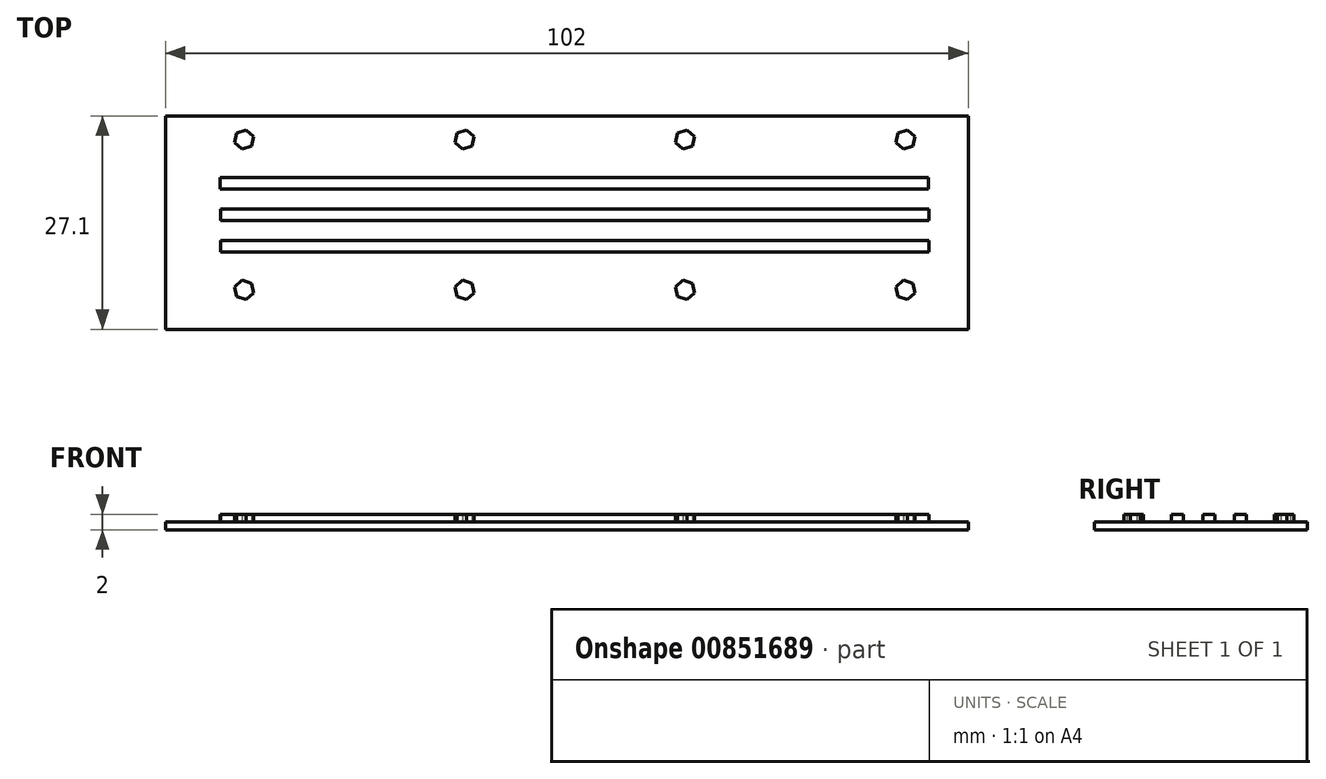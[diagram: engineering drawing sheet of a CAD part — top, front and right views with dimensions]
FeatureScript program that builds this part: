
annotation { "Feature Type Name" : "Feature", "Feature Type Description" : "" }
export const myFeature = defineFeature(function(context is Context, id is Id, definition is map)
    precondition{}
    {
        {
            var Q0;
            Q0=qCreatedBy(makeId("Top.planeOp"),FACE);
            var sketch = newSketch(context, id + "F0", { "sketchPlane" : qUnion([Q0])});
            skLineSegment(sketch, "E0.bottom", {"start": v(50, -14.55) * mm, "end": v(-52, -14.55) * mm});
            skLineSegment(sketch, "E0.top", {"start": v(50, 12.55) * mm, "end": v(-52, 12.55) * mm});
            skLineSegment(sketch, "E0.left", {"start": v(50, -14.55) * mm, "end": v(50, 12.55) * mm});
            skLineSegment(sketch, "E0.right", {"start": v(-52, -14.55) * mm, "end": v(-52, 12.55) * mm});
            skLineSegment(sketch, "E1.MirrorCS", {"start": v(-126.2, 15.84) * mm, "end": v(-126.2, -15.96) * mm, "construction": true});
            skSolve(sketch);
        }
        {
            var Q0;
            Q0=makeQuery(id+"F0.imprint","IMPRINT",FACE,{"disambiguationData":[TD([[makeQuery(id+"F0.imprint","IMPRINT",EDGE,{"derivedFrom":sQuery(id+"F0.wireOp",EDGE,"E0.bottom")}),-1.0]])]});
            extrude(context, id + "F1", {"entities" : qUnion([Q0]), "depth" : 1 * mm, "offsetDistance" : 25 * mm});
        }
        {
            var Q0;
            Q0=makeQuery(id+"F1.opExtrude","CAP_FACE",FACE,{"disambiguationData":[OSD([sQuery(id+"F0.wireOp",EDGE,"E0.bottom"),sQuery(id+"F0.wireOp",EDGE,"E0.top"),sQuery(id+"F0.wireOp",EDGE,"E0.left"),sQuery(id+"F0.wireOp",EDGE,"E0.right"),sQuery(id+"F0.wireOp",EDGE,"f0fb288a-a811-4cf8-ac7b-5b0ab74712d8.0.1.0"),sQuery(id+"F0.wireOp",EDGE,"f0fb288a-a811-4cf8-ac7b-5b0ab74712d8.0.1.2"),sQuery(id+"F0.wireOp",EDGE,"f0fb288a-a811-4cf8-ac7b-5b0ab74712d8.0.1.3"),sQuery(id+"F0.wireOp",EDGE,"f0fb288a-a811-4cf8-ac7b-5b0ab74712d8.0.2.0"),sQuery(id+"F0.wireOp",EDGE,"f0fb288a-a811-4cf8-ac7b-5b0ab74712d8.0.2.2"),sQuery(id+"F0.wireOp",EDGE,"f0fb288a-a811-4cf8-ac7b-5b0ab74712d8.0.2.3"),sQuery(id+"F0.wireOp",EDGE,"f0fb288a-a811-4cf8-ac7b-5b0ab74712d8.0.3.0"),sQuery(id+"F0.wireOp",EDGE,"f0fb288a-a811-4cf8-ac7b-5b0ab74712d8.0.3.2"),sQuery(id+"F0.wireOp",EDGE,"f0fb288a-a811-4cf8-ac7b-5b0ab74712d8.0.3.3"),sQuery(id+"F0.wireOp",EDGE,"f0fb288a-a811-4cf8-ac7b-5b0ab74712d8.0.4.0"),sQuery(id+"F0.wireOp",EDGE,"f0fb288a-a811-4cf8-ac7b-5b0ab74712d8.0.4.2"),sQuery(id+"F0.wireOp",EDGE,"f0fb288a-a811-4cf8-ac7b-5b0ab74712d8.0.4.3"),sQuery(id+"F0.wireOp",EDGE,"RKnVQM72-ZrRu-pSdJ-AaKB-wKwvzhgqjjUU"),sQuery(id+"F0.wireOp",EDGE,"7q8Byt5Z-z77J-wEaE-JFo7-deLDxunnqvEf"),sQuery(id+"F0.wireOp",EDGE,"hnmrVM6Z-fPP9-FfmX-qtFs-U7qnaTaGnJsT"),sQuery(id+"F0.wireOp",EDGE,"2AhRkgEB-YtaR-VW2O-F7jD-dwlzht8Cownv")])],"isStart":false});
            var sketch = newSketch(context, id + "F2", { "sketchPlane" : qUnion([Q0])});
            skCircle(sketch, "E2.cCircle", {"center": v(-42, 9.55) * mm, "radius": 1.25 * mm, "construction": true});
            skLineSegment(sketch, "E2.0", {"start": v(-41.07, 8.72) * mm, "end": v(-42.25, 8.33) * mm});
            skLineSegment(sketch, "E2.1", {"start": v(-42.25, 8.33) * mm, "end": v(-43.19, 9.16) * mm});
            skLineSegment(sketch, "E2.2", {"start": v(-43.19, 9.16) * mm, "end": v(-42.93, 10.38) * mm});
            skLineSegment(sketch, "E2.3", {"start": v(-42.93, 10.38) * mm, "end": v(-41.75, 10.77) * mm});
            skLineSegment(sketch, "E2.4", {"start": v(-41.75, 10.77) * mm, "end": v(-40.81, 9.94) * mm});
            skLineSegment(sketch, "E2.5", {"start": v(-40.81, 9.94) * mm, "end": v(-41.07, 8.72) * mm});
            skLineSegment(sketch, "E3.1.0.0", {"start": v(-12.81, 9.94) * mm, "end": v(-13.07, 8.72) * mm});
            skLineSegment(sketch, "E3.1.0.1", {"start": v(-13.75, 10.77) * mm, "end": v(-12.81, 9.94) * mm});
            skLineSegment(sketch, "E3.1.0.2", {"start": v(-14.93, 10.38) * mm, "end": v(-13.75, 10.77) * mm});
            skLineSegment(sketch, "E3.1.0.3", {"start": v(-15.19, 9.16) * mm, "end": v(-14.93, 10.38) * mm});
            skLineSegment(sketch, "E3.1.0.4", {"start": v(-14.25, 8.33) * mm, "end": v(-15.19, 9.16) * mm});
            skLineSegment(sketch, "E3.1.0.5", {"start": v(-13.07, 8.72) * mm, "end": v(-14.25, 8.33) * mm});
            skCircle(sketch, "E3.1.0.6", {"center": v(-14, 9.55) * mm, "radius": 1.25 * mm, "construction": true});
            skLineSegment(sketch, "E3.2.0.0", {"start": v(15.19, 9.94) * mm, "end": v(14.93, 8.72) * mm});
            skLineSegment(sketch, "E3.2.0.1", {"start": v(14.25, 10.77) * mm, "end": v(15.19, 9.94) * mm});
            skLineSegment(sketch, "E3.2.0.2", {"start": v(13.07, 10.38) * mm, "end": v(14.25, 10.77) * mm});
            skLineSegment(sketch, "E3.2.0.3", {"start": v(12.81, 9.16) * mm, "end": v(13.07, 10.38) * mm});
            skLineSegment(sketch, "E3.2.0.4", {"start": v(13.75, 8.33) * mm, "end": v(12.81, 9.16) * mm});
            skLineSegment(sketch, "E3.2.0.5", {"start": v(14.93, 8.72) * mm, "end": v(13.75, 8.33) * mm});
            skCircle(sketch, "E3.2.0.6", {"center": v(14, 9.55) * mm, "radius": 1.25 * mm, "construction": true});
            skLineSegment(sketch, "E3.3.0.0", {"start": v(43.19, 9.94) * mm, "end": v(42.93, 8.72) * mm});
            skLineSegment(sketch, "E3.3.0.1", {"start": v(42.25, 10.77) * mm, "end": v(43.19, 9.94) * mm});
            skLineSegment(sketch, "E3.3.0.2", {"start": v(41.07, 10.38) * mm, "end": v(42.25, 10.77) * mm});
            skLineSegment(sketch, "E3.3.0.3", {"start": v(40.81, 9.16) * mm, "end": v(41.07, 10.38) * mm});
            skLineSegment(sketch, "E3.3.0.4", {"start": v(41.75, 8.33) * mm, "end": v(40.81, 9.16) * mm});
            skLineSegment(sketch, "E3.3.0.5", {"start": v(42.93, 8.72) * mm, "end": v(41.75, 8.33) * mm});
            skCircle(sketch, "E3.3.0.6", {"center": v(42, 9.55) * mm, "radius": 1.25 * mm, "construction": true});
            skLineSegment(sketch, "E3.direction1", {"start": v(-41.07, 8.72) * mm, "end": v(-13.07, 8.72) * mm, "construction": true});
            skLineSegment(sketch, "E4.MirrorCS", {"start": v(-42.93, -10.38) * mm, "end": v(-41.75, -10.77) * mm});
            skLineSegment(sketch, "E5.MirrorCS", {"start": v(-15.19, -9.16) * mm, "end": v(-14.93, -10.38) * mm});
            skLineSegment(sketch, "E6.MirrorCS", {"start": v(41.75, -8.33) * mm, "end": v(40.81, -9.16) * mm});
            skLineSegment(sketch, "E7.MirrorCS", {"start": v(42.25, -10.77) * mm, "end": v(43.19, -9.94) * mm});
            skLineSegment(sketch, "E8.MirrorCS", {"start": v(12.81, -9.16) * mm, "end": v(13.07, -10.38) * mm});
            skLineSegment(sketch, "E9.MirrorCS", {"start": v(40.81, -9.16) * mm, "end": v(41.07, -10.38) * mm});
            skLineSegment(sketch, "E10.MirrorCS", {"start": v(13.07, -10.38) * mm, "end": v(14.25, -10.77) * mm});
            skLineSegment(sketch, "E11.MirrorCS", {"start": v(-14.25, -8.33) * mm, "end": v(-15.19, -9.16) * mm});
            skLineSegment(sketch, "E12.MirrorCS", {"start": v(-14.93, -10.38) * mm, "end": v(-13.75, -10.77) * mm});
            skLineSegment(sketch, "E13.MirrorCS", {"start": v(41.07, -10.38) * mm, "end": v(42.25, -10.77) * mm});
            skLineSegment(sketch, "E14.MirrorCS", {"start": v(-43.19, -9.16) * mm, "end": v(-42.93, -10.38) * mm});
            skLineSegment(sketch, "E15.MirrorCS", {"start": v(-42.25, -8.33) * mm, "end": v(-43.19, -9.16) * mm});
            skLineSegment(sketch, "E16.MirrorCS", {"start": v(13.75, -8.33) * mm, "end": v(12.81, -9.16) * mm});
            skLineSegment(sketch, "E17.MirrorCS", {"start": v(14.25, -10.77) * mm, "end": v(15.19, -9.94) * mm});
            skLineSegment(sketch, "E18.MirrorCS", {"start": v(-13.75, -10.77) * mm, "end": v(-12.81, -9.94) * mm});
            skLineSegment(sketch, "E19.MirrorCS", {"start": v(-41.75, -10.77) * mm, "end": v(-40.81, -9.94) * mm});
            skLineSegment(sketch, "E20.MirrorCS", {"start": v(-41.07, -8.72) * mm, "end": v(-42.25, -8.33) * mm});
            skLineSegment(sketch, "E21.MirrorCS", {"start": v(-13.07, -8.72) * mm, "end": v(-14.25, -8.33) * mm});
            skLineSegment(sketch, "E22.MirrorCS", {"start": v(-40.81, -9.94) * mm, "end": v(-41.07, -8.72) * mm});
            skLineSegment(sketch, "E23.MirrorCS", {"start": v(15.19, -9.94) * mm, "end": v(14.93, -8.72) * mm});
            skCircle(sketch, "E24.MirrorC", {"center": v(-14, -9.55) * mm, "radius": 1.25 * mm, "construction": true});
            skLineSegment(sketch, "E25.MirrorCS", {"start": v(43.19, -9.94) * mm, "end": v(42.93, -8.72) * mm});
            skCircle(sketch, "E26.MirrorC", {"center": v(14, -9.55) * mm, "radius": 1.25 * mm, "construction": true});
            skCircle(sketch, "E27.MirrorC", {"center": v(42, -9.55) * mm, "radius": 1.25 * mm, "construction": true});
            skLineSegment(sketch, "E28.MirrorCS", {"start": v(-41.07, -8.72) * mm, "end": v(-13.07, -8.72) * mm, "construction": true});
            skCircle(sketch, "E29.MirrorC", {"center": v(-42, -9.55) * mm, "radius": 1.25 * mm, "construction": true});
            skLineSegment(sketch, "E30.MirrorCS", {"start": v(-12.81, -9.94) * mm, "end": v(-13.07, -8.72) * mm});
            skLineSegment(sketch, "E31.MirrorCS", {"start": v(14.93, -8.72) * mm, "end": v(13.75, -8.33) * mm});
            skLineSegment(sketch, "E32.MirrorCS", {"start": v(42.93, -8.72) * mm, "end": v(41.75, -8.33) * mm});
            skLineSegment(sketch, "E33.bottom", {"start": v(45, 0.75) * mm, "end": v(-45, 0.75) * mm});
            skLineSegment(sketch, "E33.top", {"start": v(45, -0.75) * mm, "end": v(-45, -0.75) * mm});
            skLineSegment(sketch, "E33.left", {"start": v(45, 0.75) * mm, "end": v(45, -0.75) * mm});
            skLineSegment(sketch, "E33.right", {"start": v(-45, 0.75) * mm, "end": v(-45, -0.75) * mm});
            skPoint(sketch, "E33.middle", {"position": v(0, 0) * mm});
            skLineSegment(sketch, "E34.1.0.0", {"start": v(45, -3.25) * mm, "end": v(-45, -3.25) * mm});
            skLineSegment(sketch, "E34.1.0.1", {"start": v(-45, -3.25) * mm, "end": v(-45, -4.75) * mm});
            skLineSegment(sketch, "E34.1.0.2", {"start": v(45, -4.75) * mm, "end": v(-45, -4.75) * mm});
            skLineSegment(sketch, "E34.1.0.3", {"start": v(45, -3.25) * mm, "end": v(45, -4.75) * mm});
            skLineSegment(sketch, "E35.1.0.1", {"start": v(44.93, 3.25) * mm, "end": v(-45.07, 3.25) * mm});
            skLineSegment(sketch, "E35.1.0.2", {"start": v(44.93, 4.75) * mm, "end": v(-45.07, 4.75) * mm});
            skLineSegment(sketch, "E35.1.0.3", {"start": v(44.93, 4.75) * mm, "end": v(44.93, 3.25) * mm});
            skLineSegment(sketch, "E36", {"start": v(-45.07, 4.75) * mm, "end": v(-45.07, 3.25) * mm});
            skSolve(sketch);
        }
        {
            var Q0;
            Q0=makeQuery(id+"F2.imprint","IMPRINT",FACE,{"disambiguationData":[TD([[makeQuery(id+"F2.imprint","IMPRINT",EDGE,{"derivedFrom":sQuery(id+"F2.wireOp",EDGE,"E2.0")}),-1.0]])]});
            var Q1;
            Q1=makeQuery(id+"F2.imprint","IMPRINT",FACE,{"disambiguationData":[TD([[makeQuery(id+"F2.imprint","IMPRINT",EDGE,{"derivedFrom":sQuery(id+"F2.wireOp",EDGE,"E3.1.0.0")}),-1.0]])]});
            var Q2;
            Q2=makeQuery(id+"F2.imprint","IMPRINT",FACE,{"disambiguationData":[TD([[makeQuery(id+"F2.imprint","IMPRINT",EDGE,{"derivedFrom":sQuery(id+"F2.wireOp",EDGE,"E3.2.0.0")}),-1.0]])]});
            var Q3;
            Q3=makeQuery(id+"F2.imprint","IMPRINT",FACE,{"disambiguationData":[TD([[makeQuery(id+"F2.imprint","IMPRINT",EDGE,{"derivedFrom":sQuery(id+"F2.wireOp",EDGE,"E3.3.0.0")}),-1.0]])]});
            var Q4;
            Q4=makeQuery(id+"F2.imprint","IMPRINT",FACE,{"disambiguationData":[TD([[makeQuery(id+"F2.imprint","IMPRINT",EDGE,{"derivedFrom":sQuery(id+"F2.wireOp",EDGE,"E4.MirrorCS")}),1.0]])]});
            var Q5;
            Q5=makeQuery(id+"F2.imprint","IMPRINT",FACE,{"disambiguationData":[TD([[makeQuery(id+"F2.imprint","IMPRINT",EDGE,{"derivedFrom":sQuery(id+"F2.wireOp",EDGE,"E5.MirrorCS")}),1.0]])]});
            var Q6;
            Q6=makeQuery(id+"F2.imprint","IMPRINT",FACE,{"disambiguationData":[TD([[makeQuery(id+"F2.imprint","IMPRINT",EDGE,{"derivedFrom":sQuery(id+"F2.wireOp",EDGE,"E8.MirrorCS")}),1.0]])]});
            var Q7;
            Q7=makeQuery(id+"F2.imprint","IMPRINT",FACE,{"disambiguationData":[TD([[makeQuery(id+"F2.imprint","IMPRINT",EDGE,{"derivedFrom":sQuery(id+"F2.wireOp",EDGE,"E6.MirrorCS")}),1.0]])]});
            var Q8;
            Q8=makeQuery(id+"F2.imprint","IMPRINT",FACE,{"disambiguationData":[TD([[makeQuery(id+"F2.imprint","IMPRINT",EDGE,{"derivedFrom":sQuery(id+"F2.wireOp",EDGE,"E35.2.0.1")}),-1.0]])]});
            var Q9;
            Q9=makeQuery(id+"F2.imprint","IMPRINT",FACE,{"disambiguationData":[TD([[makeQuery(id+"F2.imprint","IMPRINT",EDGE,{"derivedFrom":sQuery(id+"F2.wireOp",EDGE,"E35.1.0.1")}),-1.0]])]});
            var Q10;
            Q10=makeQuery(id+"F2.imprint","IMPRINT",FACE,{"disambiguationData":[TD([[makeQuery(id+"F2.imprint","IMPRINT",EDGE,{"derivedFrom":sQuery(id+"F2.wireOp",EDGE,"E33.bottom")}),1.0]])]});
            var Q11;
            Q11=makeQuery(id+"F2.imprint","IMPRINT",FACE,{"disambiguationData":[TD([[makeQuery(id+"F2.imprint","IMPRINT",EDGE,{"derivedFrom":sQuery(id+"F2.wireOp",EDGE,"E34.1.0.0")}),1.0]])]});
            var Q12;
            Q12=makeQuery(id+"F2.imprint","IMPRINT",FACE,{"disambiguationData":[TD([[makeQuery(id+"F2.imprint","IMPRINT",EDGE,{"derivedFrom":sQuery(id+"F2.wireOp",EDGE,"E34.2.0.0")}),1.0]])]});
            extrude(context, id + "F3", {"entities" : qUnion([Q0, Q1, Q2, Q3, Q4, Q5, Q6, Q7, Q8, Q9, Q10, Q11, Q12]), "operationType" : NewBodyOperationType.ADD, "depth" : 1 * mm, "offsetDistance" : 25 * mm});
        }
    });
